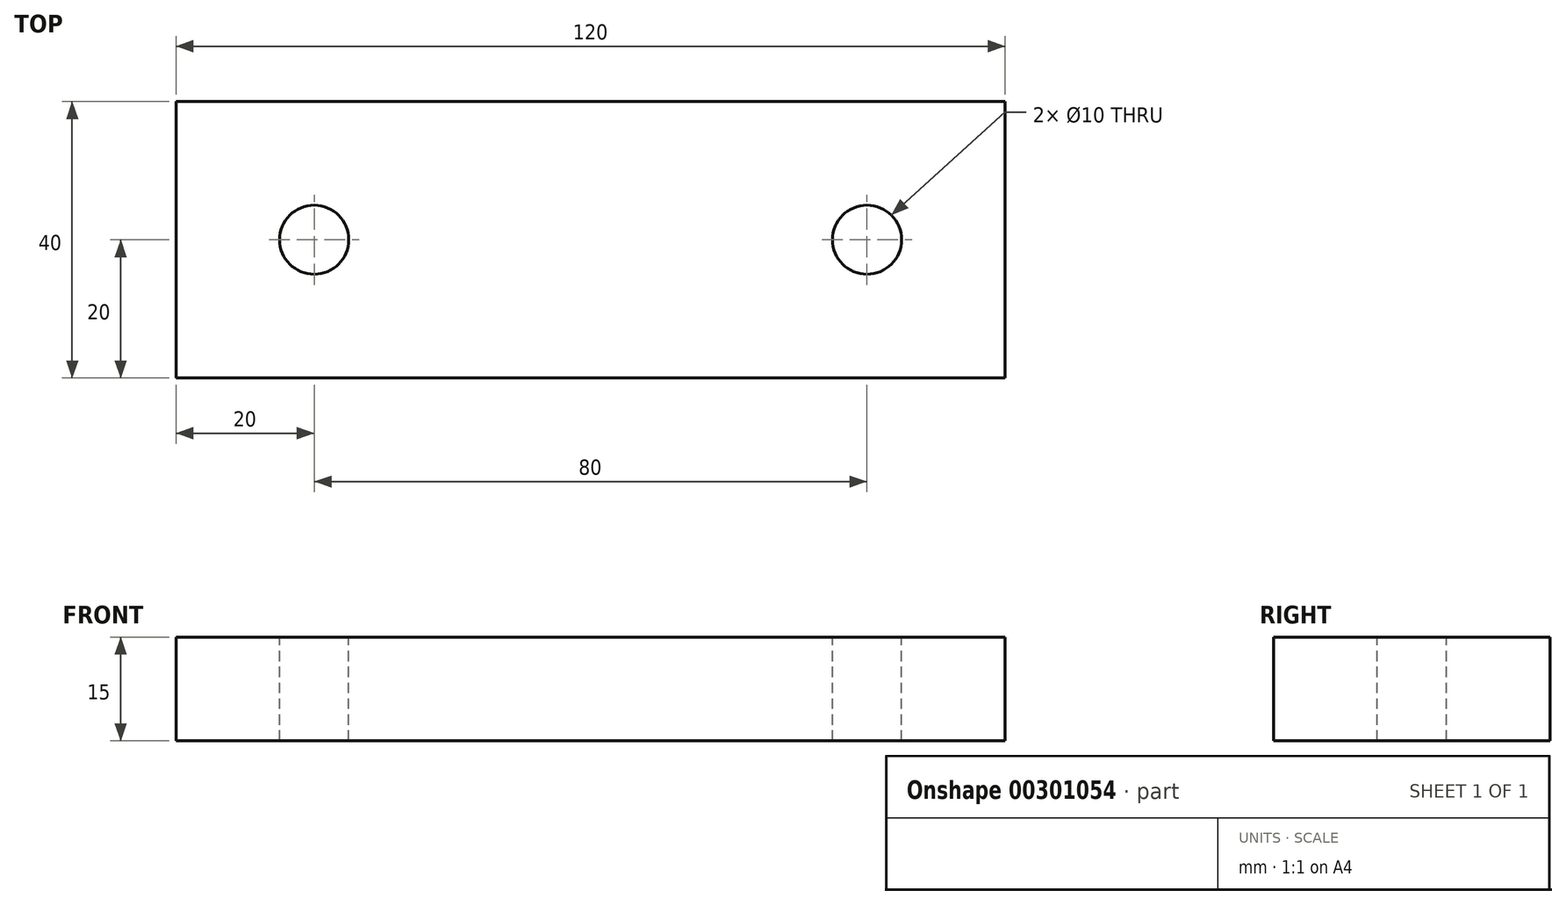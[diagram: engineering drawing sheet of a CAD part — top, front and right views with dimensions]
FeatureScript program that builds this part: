
annotation { "Feature Type Name" : "Feature", "Feature Type Description" : "" }
export const myFeature = defineFeature(function(context is Context, id is Id, definition is map)
    precondition{}
    {
        {
            var Q0;
            Q0=qCreatedBy(makeId("Front.planeOp"),FACE);
            var sketch = newSketch(context, id + "F0", { "sketchPlane" : qUnion([Q0])});
            skLineSegment(sketch, "E0", {"start": v(0, 0) * mm, "end": v(120, 0) * mm});
            skLineSegment(sketch, "E1", {"start": v(120, 0) * mm, "end": v(120, 15) * mm});
            skLineSegment(sketch, "E2", {"start": v(120, 15) * mm, "end": v(0, 15) * mm});
            skLineSegment(sketch, "E3", {"start": v(0, 15) * mm, "end": v(0, 0) * mm});
            skSolve(sketch);
        }
        {
            var Q0;
            Q0=makeQuery(id+"F0.imprint","IMPRINT",FACE,{"disambiguationData":[TD([[makeQuery(id+"F0.imprint","IMPRINT",EDGE,{"derivedFrom":sQuery(id+"F0.wireOp",EDGE,"E0")}),1.0]])]});
            extrude(context, id + "F1", {"entities" : qUnion([Q0]), "depth" : 40 * mm});
        }
        {
            var Q0;
            Q0=makeQuery(id+"F1.opExtrude","SWEPT_FACE",FACE,{"disambiguationData":[OSD([sQuery(id+"F0.wireOp",EDGE,"E2")])]});
            var sketch = newSketch(context, id + "F2", { "sketchPlane" : qUnion([Q0])});
            skCircle(sketch, "E4", {"center": v(20, -20) * mm, "radius": 5 * mm});
            skCircle(sketch, "E5", {"center": v(100, -20) * mm, "radius": 5 * mm});
            skSolve(sketch);
        }
        {
            var Q0;
            Q0=makeQuery(id+"F2.imprint","IMPRINT",FACE,{"disambiguationData":[TD([[makeQuery(id+"F2.imprint","IMPRINT",EDGE,{"derivedFrom":sQuery(id+"F2.wireOp",EDGE,"E4")}),1.0]])]});
            var Q1;
            Q1=makeQuery(id+"F2.imprint","IMPRINT",FACE,{"disambiguationData":[TD([[makeQuery(id+"F2.imprint","IMPRINT",EDGE,{"derivedFrom":sQuery(id+"F2.wireOp",EDGE,"E5")}),1.0]])]});
            extrude(context, id + "F3", {"entities" : qUnion([Q0, Q1]), "operationType" : NewBodyOperationType.REMOVE, "endBound" : BoundingType.THROUGH_ALL, "oppositeDirection" : true, "depth" : 25 * mm});
        }
    });
